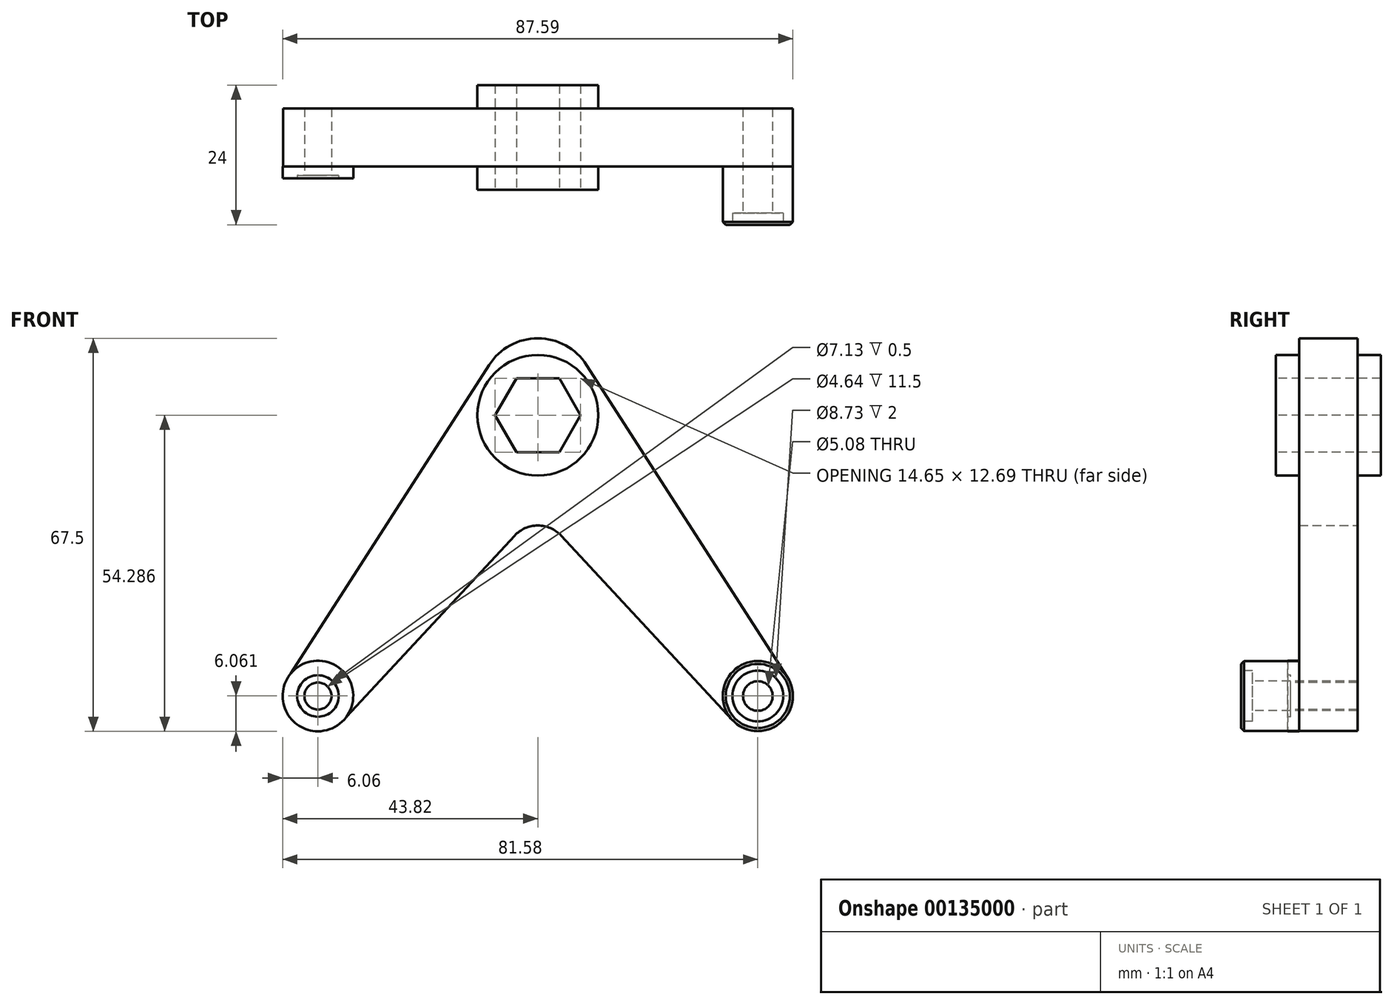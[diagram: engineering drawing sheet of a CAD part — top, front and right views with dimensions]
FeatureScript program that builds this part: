
annotation { "Feature Type Name" : "Feature", "Feature Type Description" : "" }
export const myFeature = defineFeature(function(context is Context, id is Id, definition is map)
    precondition{}
    {
        {
            var Q0;
            Q0=qCreatedBy(makeId("Front.planeOp"),FACE);
            var sketch = newSketch(context, id + "F0", { "sketchPlane" : qUnion([Q0])});
            skArc(sketch, "E0", {"start": v(8.36, 41.94) * mm, "mid": v(0, 46.5) * mm, "end": v(-8.36, 41.94) * mm});
            skArc(sketch, "E1", {"start": v(-42.82, -11.69) * mm, "mid": v(-41.44, -19.7) * mm, "end": v(-33.35, -19.03) * mm});
            skArc(sketch, "E2.MirrorC", {"start": v(42.82, -11.69) * mm, "mid": v(41.44, -19.7) * mm, "end": v(33.35, -19.03) * mm});
            skArc(sketch, "E3", {"start": v(4, 12.6) * mm, "mid": v(0, 14.35) * mm, "end": v(-4, 12.6) * mm});
            skLineSegment(sketch, "E4", {"start": v(-42.82, -11.69) * mm, "end": v(-8.36, 41.94) * mm});
            skLineSegment(sketch, "E5", {"start": v(-33.35, -19.03) * mm, "end": v(-4, 12.6) * mm});
            skLineSegment(sketch, "E6", {"start": v(4, 12.6) * mm, "end": v(33.35, -19.03) * mm});
            skLineSegment(sketch, "E7", {"start": v(8.36, 41.94) * mm, "end": v(42.82, -11.69) * mm});
            skSolve(sketch);
        }
        {
            var Q0;
            Q0 = qSketchRegion(id + "F0", true);
            extrude(context, id + "F1", {"entities" : qUnion([Q0]), "depth" : 10 * mm});
        }
        {
            var Q0;
            Q0=makeQuery(id+"F1.opExtrude","CAP_FACE",FACE,{"disambiguationData":[OSD([sQuery(id+"F0.wireOp",EDGE,"E0"),sQuery(id+"F0.wireOp",EDGE,"E1"),sQuery(id+"F0.wireOp",EDGE,"E2.MirrorC"),sQuery(id+"F0.wireOp",EDGE,"E3"),sQuery(id+"F0.wireOp",EDGE,"E4"),sQuery(id+"F0.wireOp",EDGE,"E5"),sQuery(id+"F0.wireOp",EDGE,"E6"),sQuery(id+"F0.wireOp",EDGE,"E7")])],"isStart":false});
            var sketch = newSketch(context, id + "F2", { "sketchPlane" : qUnion([Q0])});
            skCircle(sketch, "E8", {"center": v(0, 33.29) * mm, "radius": 10.37 * mm});
            skSolve(sketch);
        }
        {
            var Q0;
            Q0 = qSketchRegion(id + "F2", true);
            extrude(context, id + "F3", {"entities" : qUnion([Q0]), "operationType" : NewBodyOperationType.ADD, "depth" : 4 * mm, "hasSecondDirection" : true, "secondDirectionOppositeDirection" : true, "secondDirectionDepth" : 14 * mm});
        }
        {
            var Q0;
            Q0=makeQuery(id+"F3.opExtrude","CAP_FACE",FACE,{"disambiguationData":[OSD([sQuery(id+"F2.wireOp",EDGE,"E8")])],"isStart":false});
            var sketch = newSketch(context, id + "F4", { "sketchPlane" : qUnion([Q0])});
            skCircle(sketch, "E9.cCircle", {"center": v(0, 33.29) * mm, "radius": 6.34 * mm, "construction": true});
            skLineSegment(sketch, "E9.0", {"start": v(3.66, 26.94) * mm, "end": v(-3.66, 26.94) * mm});
            skLineSegment(sketch, "E9.1", {"start": v(-3.66, 26.94) * mm, "end": v(-7.32, 33.29) * mm});
            skLineSegment(sketch, "E9.2", {"start": v(-7.32, 33.29) * mm, "end": v(-3.66, 39.63) * mm});
            skLineSegment(sketch, "E9.3", {"start": v(-3.66, 39.63) * mm, "end": v(3.66, 39.63) * mm});
            skLineSegment(sketch, "E9.4", {"start": v(3.66, 39.63) * mm, "end": v(7.32, 33.29) * mm});
            skLineSegment(sketch, "E9.5", {"start": v(7.32, 33.29) * mm, "end": v(3.66, 26.94) * mm});
            skPoint(sketch, "E9.0.midPoint", {"position": v(0, 26.94) * mm});
            skSolve(sketch);
        }
        {
            var Q0;
            Q0 = qSketchRegion(id + "F4", true);
            extrude(context, id + "F5", {"entities" : qUnion([Q0]), "operationType" : NewBodyOperationType.REMOVE, "oppositeDirection" : true, "depth" : 25 * mm});
        }
        {
            var Q0;
            Q0=makeQuery(id+"F1.opExtrude","CAP_FACE",FACE,{"disambiguationData":[OSD([sQuery(id+"F0.wireOp",EDGE,"E0"),sQuery(id+"F0.wireOp",EDGE,"E1"),sQuery(id+"F0.wireOp",EDGE,"E2.MirrorC"),sQuery(id+"F0.wireOp",EDGE,"E3"),sQuery(id+"F0.wireOp",EDGE,"E4"),sQuery(id+"F0.wireOp",EDGE,"E5"),sQuery(id+"F0.wireOp",EDGE,"E6"),sQuery(id+"F0.wireOp",EDGE,"E7")])],"isStart":false});
            var sketch = newSketch(context, id + "F6", { "sketchPlane" : qUnion([Q0])});
            skCircle(sketch, "E10", {"center": v(-37.76, -14.94) * mm, "radius": 6.06 * mm});
            skSolve(sketch);
        }
        {
            var Q0;
            Q0 = qSketchRegion(id + "F6", true);
            extrude(context, id + "F7", {"entities" : qUnion([Q0]), "operationType" : NewBodyOperationType.ADD, "depth" : 2 * mm});
        }
        {
            var Q0;
            Q0=makeQuery(id+"F7.opExtrude","CAP_FACE",FACE,{"disambiguationData":[OSD([sQuery(id+"F6.wireOp",EDGE,"E10")])],"isStart":false});
            var sketch = newSketch(context, id + "F8", { "sketchPlane" : qUnion([Q0])});
            skCircle(sketch, "E11", {"center": v(-37.76, -14.94) * mm, "radius": 3.57 * mm});
            skSolve(sketch);
        }
        {
            var Q0;
            Q0 = qSketchRegion(id + "F8", true);
            extrude(context, id + "F9", {"entities" : qUnion([Q0]), "operationType" : NewBodyOperationType.REMOVE, "oppositeDirection" : true, "depth" : .5 * mm});
        }
        {
            var Q0;
            Q0=makeQuery(id+"F9.boolean.opBoolean","COPY",FACE,{"derivedFrom":makeQuery(id+"F9.opExtrude","CAP_FACE",FACE,{"disambiguationData":[OSD([sQuery(id+"F8.wireOp",EDGE,"E11")])],"isStart":false})});
            var sketch = newSketch(context, id + "F10", { "sketchPlane" : qUnion([Q0])});
            skCircle(sketch, "E12", {"center": v(-37.76, -14.94) * mm, "radius": 2.32 * mm});
            skSolve(sketch);
        }
        {
            var Q0;
            Q0 = qSketchRegion(id + "F10", true);
            extrude(context, id + "F11", {"entities" : qUnion([Q0]), "operationType" : NewBodyOperationType.REMOVE, "oppositeDirection" : true, "depth" : 25 * mm});
        }
        {
            var Q0;
            Q0=makeQuery(id+"F1.opExtrude","CAP_FACE",FACE,{"disambiguationData":[OSD([sQuery(id+"F0.wireOp",EDGE,"E0"),sQuery(id+"F0.wireOp",EDGE,"E1"),sQuery(id+"F0.wireOp",EDGE,"E2.MirrorC"),sQuery(id+"F0.wireOp",EDGE,"E3"),sQuery(id+"F0.wireOp",EDGE,"E4"),sQuery(id+"F0.wireOp",EDGE,"E5"),sQuery(id+"F0.wireOp",EDGE,"E6"),sQuery(id+"F0.wireOp",EDGE,"E7")])],"isStart":false});
            var sketch = newSketch(context, id + "F12", { "sketchPlane" : qUnion([Q0])});
            skCircle(sketch, "E13", {"center": v(37.76, -14.94) * mm, "radius": 6 * mm});
            skSolve(sketch);
        }
        {
            var Q0;
            Q0 = qSketchRegion(id + "F12", true);
            extrude(context, id + "F13", {"entities" : qUnion([Q0]), "operationType" : NewBodyOperationType.ADD, "depth" : 10 * mm});
        }
        {
            var Q0;
            Q0=makeQuery(id+"F13.opExtrude","CAP_FACE",FACE,{"disambiguationData":[OSD([sQuery(id+"F12.wireOp",EDGE,"E13")])],"isStart":false});
            var sketch = newSketch(context, id + "F14", { "sketchPlane" : qUnion([Q0])});
            skCircle(sketch, "E14", {"center": v(37.76, -14.94) * mm, "radius": 4.36 * mm});
            skSolve(sketch);
        }
        {
            var Q0;
            Q0 = qSketchRegion(id + "F14", true);
            extrude(context, id + "F15", {"entities" : qUnion([Q0]), "operationType" : NewBodyOperationType.REMOVE, "oppositeDirection" : true, "depth" : 2 * mm});
        }
        {
            var Q0;
            Q0=makeQuery(id+"F13.opExtrude","CAP_EDGE",EDGE,{"disambiguationData":[OSD([sQuery(id+"F12.wireOp",EDGE,"E13")])],"isStart":false});
            chamfer(context, id + "F16", {"entities" : qUnion([Q0]), "width" : .5 * mm, "tangentPropagation" : true});
        }
        {
            var Q0;
            Q0=makeQuery(id+"F15.boolean.opBoolean","COPY",FACE,{"derivedFrom":makeQuery(id+"F15.opExtrude","CAP_FACE",FACE,{"disambiguationData":[OSD([sQuery(id+"F14.wireOp",EDGE,"E14")])],"isStart":false})});
            var sketch = newSketch(context, id + "F17", { "sketchPlane" : qUnion([Q0])});
            skCircle(sketch, "E15", {"center": v(37.76, -14.94) * mm, "radius": 2.54 * mm});
            skSolve(sketch);
        }
        {
            var Q0;
            Q0 = qSketchRegion(id + "F17", true);
            extrude(context, id + "F18", {"entities" : qUnion([Q0]), "operationType" : NewBodyOperationType.REMOVE, "oppositeDirection" : true, "depth" : 25 * mm});
        }
    });
